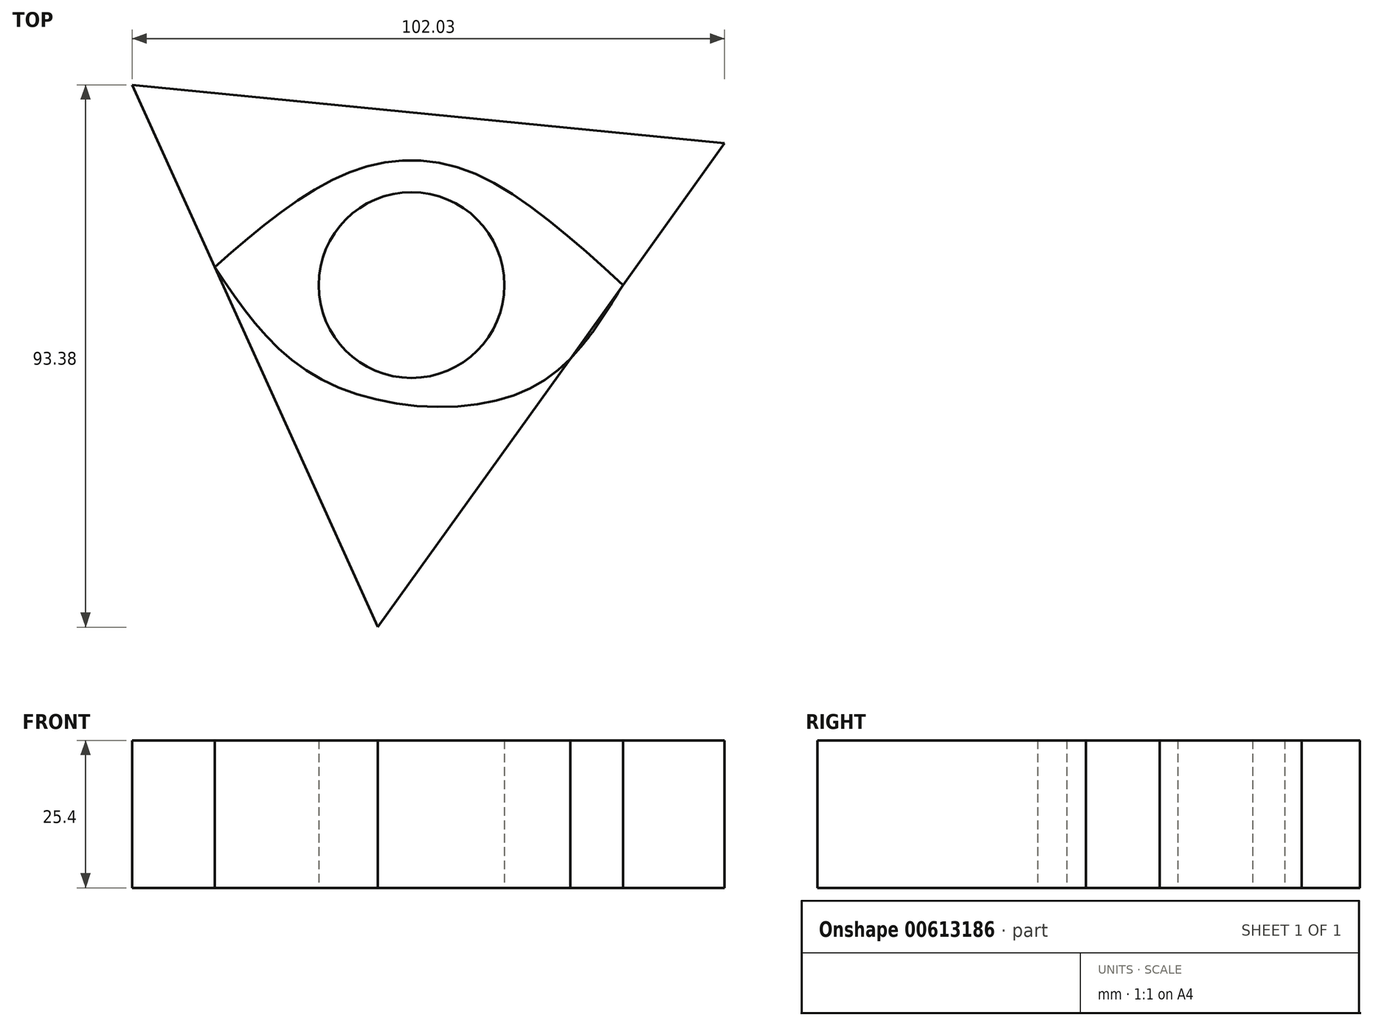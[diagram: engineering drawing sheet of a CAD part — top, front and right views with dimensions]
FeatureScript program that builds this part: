
annotation { "Feature Type Name" : "Feature", "Feature Type Description" : "" }
export const myFeature = defineFeature(function(context is Context, id is Id, definition is map)
    precondition{}
    {
        {
            var Q0;
            Q0=qCreatedBy(makeId("Top.planeOp"),FACE);
            var sketch = newSketch(context, id + "F0", { "sketchPlane" : qUnion([Q0])});
            skCircle(sketch, "E0.cCircle", {"center": v(0, 0) * mm, "radius": 29.6 * mm, "construction": true});
            skLineSegment(sketch, "E0.0", {"start": v(53.91, 24.43) * mm, "end": v(-5.8, -58.9) * mm});
            skLineSegment(sketch, "E0.1", {"start": v(-5.8, -58.9) * mm, "end": v(-48.12, 34.47) * mm});
            skLineSegment(sketch, "E0.2", {"start": v(-48.12, 34.47) * mm, "end": v(53.91, 24.43) * mm});
            skPoint(sketch, "E0.0.midPoint", {"position": v(24.06, -17.24) * mm});
            skFitSpline(sketch, "E1", {"points": [v(-33.9, 3.1) * mm, v(-11.52, 19.08) * mm, v(9.3, 19.82) * mm, v(36.4, 0) * mm], "startDerivative": vector(65.41, 56.74) * mm, "endDerivative": vector(73.18, -66.76) * mm});
            skFitSpline(sketch, "E2", {"points": [v(36.4, 0) * mm, v(19.27, -18.34) * mm, v(-14.66, -16.68) * mm, v(-33.9, 3.1) * mm], "startDerivative": vector(-43.18, -71.04) * mm, "endDerivative": vector(-47.44, 70.56) * mm});
            skCircle(sketch, "E3", {"center": v(3, 0) * mm, "radius": 17.57 * mm});
            skSolve(sketch);
        }
        {
            var Q0;
            {var subQ0=sQuery(id+"F0.wireOp",EDGE,"E0.2");Q0=makeQuery(id+"F0.imprint","IMPRINT",FACE,{"disambiguationData":[TD([[makeQuery(id+"F0.imprint","IMPRINT",EDGE,{"derivedFrom":subQ0}),-1.0]])]});}
            var Q1;
            {var subQ0=sQuery(id+"F0.wireOp",EDGE,"E0.1");var subQ1=sQuery(id+"F0.wireOp",EDGE,"E0.0");var subQ2=makeQuery(id+"F0.imprint","INTERSECT",VERTEX,{"derivedFrom":[subQ1,subQ0]});Q1=makeQuery(id+"F0.imprint","IMPRINT",FACE,{"disambiguationData":[TD([[makeQuery(id+"F0.imprint","IMPRINT",EDGE,{"disambiguationData":[TD([[subQ2,1.0]])],"derivedFrom":subQ1}),-1.0]])]});}
            var Q2;
            {var subQ0=sQuery(id+"F0.wireOp",EDGE,"E2");var subQ1=sQuery(id+"F0.wireOp",EDGE,"E0.0");var subQ3=makeQuery(id+"F0.imprint","INTERSECT",VERTEX,{"derivedFrom":[subQ1,subQ0]});Q2=makeQuery(id+"F0.imprint","IMPRINT",FACE,{"disambiguationData":[TD([[makeQuery(id+"F0.imprint","IMPRINT",EDGE,{"disambiguationData":[TD([[subQ3,1.0]])],"derivedFrom":subQ1}),1.0]])]});}
            extrude(context, id + "F1", {"entities" : qUnion([Q0, Q1, Q2]), "depth" : 25.4 * mm, "offsetDistance" : 25.4 * mm});
        }
        {
            var Q0;
            Q0=qCreatedBy(makeId("Top.planeOp"),FACE);
            var sketch = newSketch(context, id + "F2", { "sketchPlane" : qUnion([Q0])});
            skCircle(sketch, "E4", {"center": v(0, 0) * mm, "radius": 16 * mm});
            skSolve(sketch);
        }
        {
            var Q0;
            Q0=makeQuery(id+"F2.imprint","IMPRINT",FACE,{"disambiguationData":[TD([[makeQuery(id+"F2.imprint","IMPRINT",EDGE,{"derivedFrom":sQuery(id+"F2.wireOp",EDGE,"E4")}),1.0]])]});
            extrude(context, id + "F3", {"entities" : qUnion([Q0]), "depth" : 25.4 * mm, "offsetDistance" : 25.4 * mm});
        }
    });
